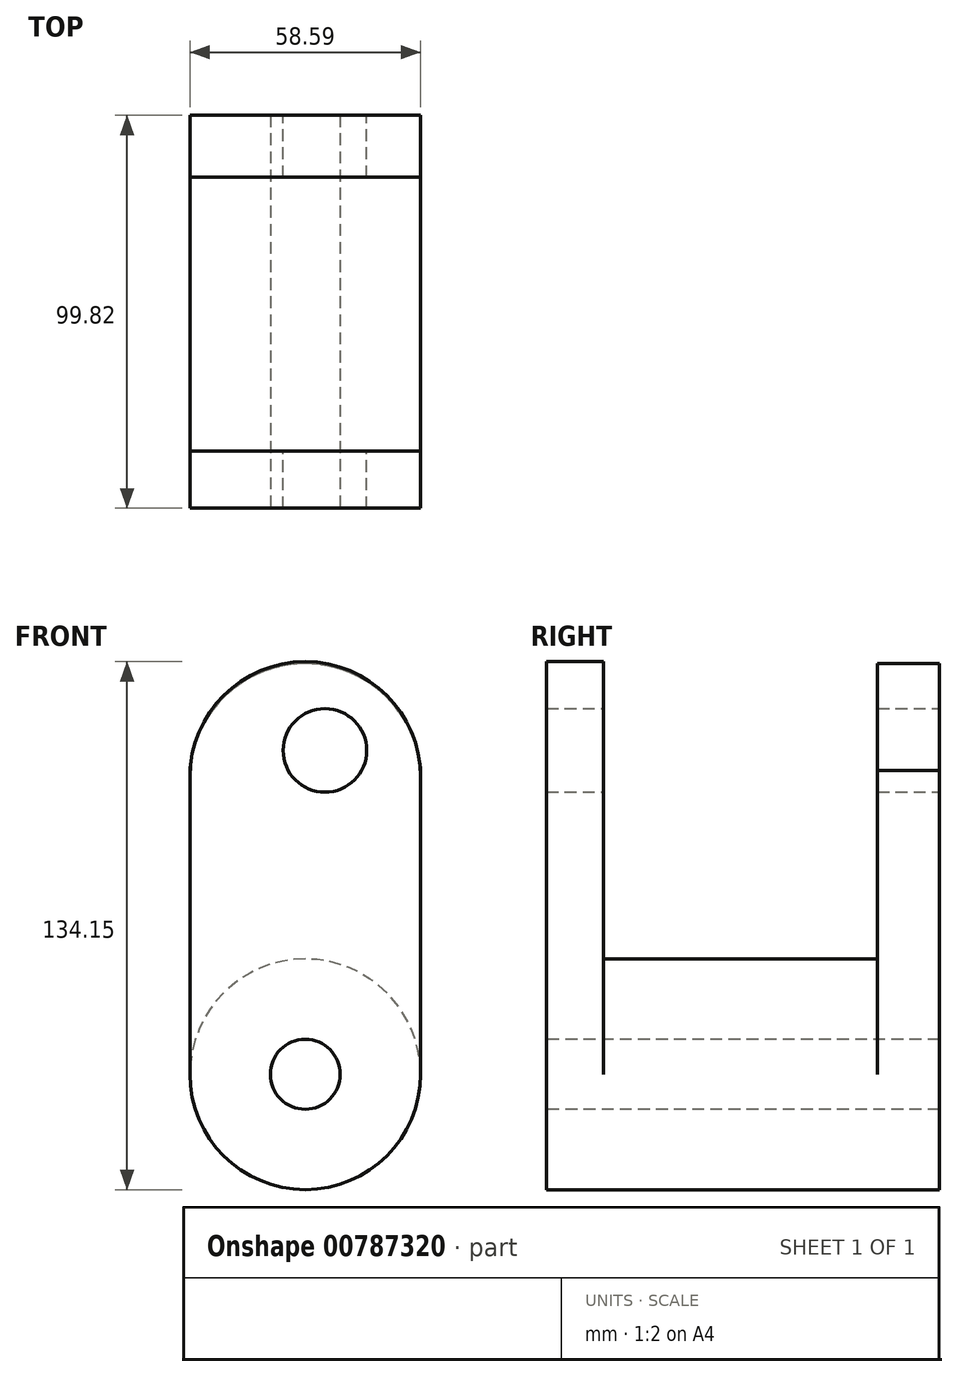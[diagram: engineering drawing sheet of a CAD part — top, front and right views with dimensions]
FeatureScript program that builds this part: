
annotation { "Feature Type Name" : "Feature", "Feature Type Description" : "" }
export const myFeature = defineFeature(function(context is Context, id is Id, definition is map)
    precondition{}
    {
        {
            var Q0;
            Q0=qCreatedBy(makeId("Front.planeOp"),FACE);
            var sketch = newSketch(context, id + "F0", { "sketchPlane" : qUnion([Q0])});
            skCircle(sketch, "E0", {"center": v(-37.7, 0) * mm, "radius": 29.3 * mm});
            skSolve(sketch);
        }
        {
            var Q0;
            Q0=makeQuery(id+"F0.imprint","IMPRINT",FACE,{"disambiguationData":[TD([[makeQuery(id+"F0.imprint","IMPRINT",EDGE,{"derivedFrom":sQuery(id+"F0.wireOp",EDGE,"E0")}),1.0]])]});
            extrude(context, id + "F1", {"entities" : qUnion([Q0]), "depth" : 99.82 * mm, "offsetDistance" : 25.4 * mm});
        }
        {
            var Q0;
            Q0=makeQuery(id+"F1.opExtrude","CAP_FACE",FACE,{"disambiguationData":[OSD([sQuery(id+"F0.wireOp",EDGE,"E0")])],"isStart":false});
            var sketch = newSketch(context, id + "F2", { "sketchPlane" : qUnion([Q0])});
            skCircle(sketch, "E1", {"center": v(-37.7, 0) * mm, "radius": 8.89 * mm});
            skSolve(sketch);
        }
        {
            var Q0;
            Q0=makeQuery(id+"F2.imprint","IMPRINT",FACE,{"disambiguationData":[TD([[makeQuery(id+"F2.imprint","IMPRINT",EDGE,{"derivedFrom":sQuery(id+"F2.wireOp",EDGE,"E1")}),1.0]])]});
            extrude(context, id + "F3", {"entities" : qUnion([Q0]), "operationType" : NewBodyOperationType.REMOVE, "oppositeDirection" : true, "depth" : 120.9 * mm, "offsetDistance" : 25.4 * mm});
        }
        {
            var Q0;
            Q0=makeQuery(id+"F1.opExtrude","CAP_FACE",FACE,{"disambiguationData":[OSD([sQuery(id+"F0.wireOp",EDGE,"E0")])],"isStart":false});
            var sketch = newSketch(context, id + "F4", { "sketchPlane" : qUnion([Q0])});
            skLineSegment(sketch, "E2", {"start": v(-67, 0) * mm, "end": v(-67, 75.55) * mm});
            skLineSegment(sketch, "E3", {"start": v(-8.4, 0) * mm, "end": v(-8.4, 75.55) * mm});
            skArc(sketch, "E4", {"start": v(-8.4, 75.55) * mm, "mid": v(-37.7, 104.85) * mm, "end": v(-67, 75.55) * mm});
            skSolve(sketch);
        }
        {
            var Q0;
            {var subQ0=sQuery(id+"F4.wireOp",EDGE,"E2");Q0=makeQuery(id+"F4.imprint","IMPRINT",FACE,{"disambiguationData":[TD([[makeQuery(id+"F4.imprint","IMPRINT",EDGE,{"derivedFrom":subQ0}),-1.0]])]});}
            extrude(context, id + "F5", {"entities" : qUnion([Q0]), "operationType" : NewBodyOperationType.ADD, "oppositeDirection" : true, "depth" : 14.48 * mm, "offsetDistance" : 25.4 * mm});
        }
        {
            var Q0;
            Q0=makeQuery(id+"F1.opExtrude","CAP_FACE",FACE,{"disambiguationData":[OSD([sQuery(id+"F0.wireOp",EDGE,"E0")])],"isStart":true});
            var sketch = newSketch(context, id + "F6", { "sketchPlane" : qUnion([Q0])});
            skLineSegment(sketch, "E5", {"start": v(8.4, 0) * mm, "end": v(8.4, 77.24) * mm});
            skLineSegment(sketch, "E6", {"start": v(67, 0) * mm, "end": v(67, 77.24) * mm});
            skArc(sketch, "E7", {"start": v(67, 77.24) * mm, "mid": v(37.7, 104.34) * mm, "end": v(8.4, 77.24) * mm});
            skSolve(sketch);
        }
        {
            var Q0;
            {var subQ0=sQuery(id+"F6.wireOp",EDGE,"E5");Q0=makeQuery(id+"F6.imprint","IMPRINT",FACE,{"disambiguationData":[TD([[makeQuery(id+"F6.imprint","IMPRINT",EDGE,{"derivedFrom":subQ0}),-1.0]])]});}
            extrude(context, id + "F7", {"entities" : qUnion([Q0]), "operationType" : NewBodyOperationType.ADD, "oppositeDirection" : true, "depth" : 15.75 * mm, "offsetDistance" : 25.4 * mm});
        }
        {
            var Q0;
            {var subQ0=sQuery(id+"F0.wireOp",EDGE,"E0");Q0=makeQuery(id+"F7.boolean.opBoolean","MERGE",FACE,{"derivedFrom":[makeQuery(id+"F1.opExtrude","CAP_FACE",FACE,{"disambiguationData":[OSD([subQ0])],"isStart":true}),makeQuery(id+"F7.opExtrude","CAP_FACE",FACE,{"disambiguationData":[OSD([subQ0,sQuery(id+"F6.wireOp",EDGE,"E5"),sQuery(id+"F6.wireOp",EDGE,"E6"),sQuery(id+"F6.wireOp",EDGE,"E7")])],"isStart":true})]});}
            var sketch = newSketch(context, id + "F8", { "sketchPlane" : qUnion([Q0])});
            skCircle(sketch, "E8", {"center": v(32.72, 82.3) * mm, "radius": 10.6 * mm});
            skSolve(sketch);
        }
        {
            var Q0;
            Q0=makeQuery(id+"F8.imprint","IMPRINT",FACE,{"disambiguationData":[TD([[makeQuery(id+"F8.imprint","IMPRINT",EDGE,{"derivedFrom":sQuery(id+"F8.wireOp",EDGE,"E8")}),1.0]])]});
            extrude(context, id + "F9", {"entities" : qUnion([Q0]), "operationType" : NewBodyOperationType.REMOVE, "oppositeDirection" : true, "depth" : 149.35 * mm, "offsetDistance" : 25.4 * mm});
        }
    });
